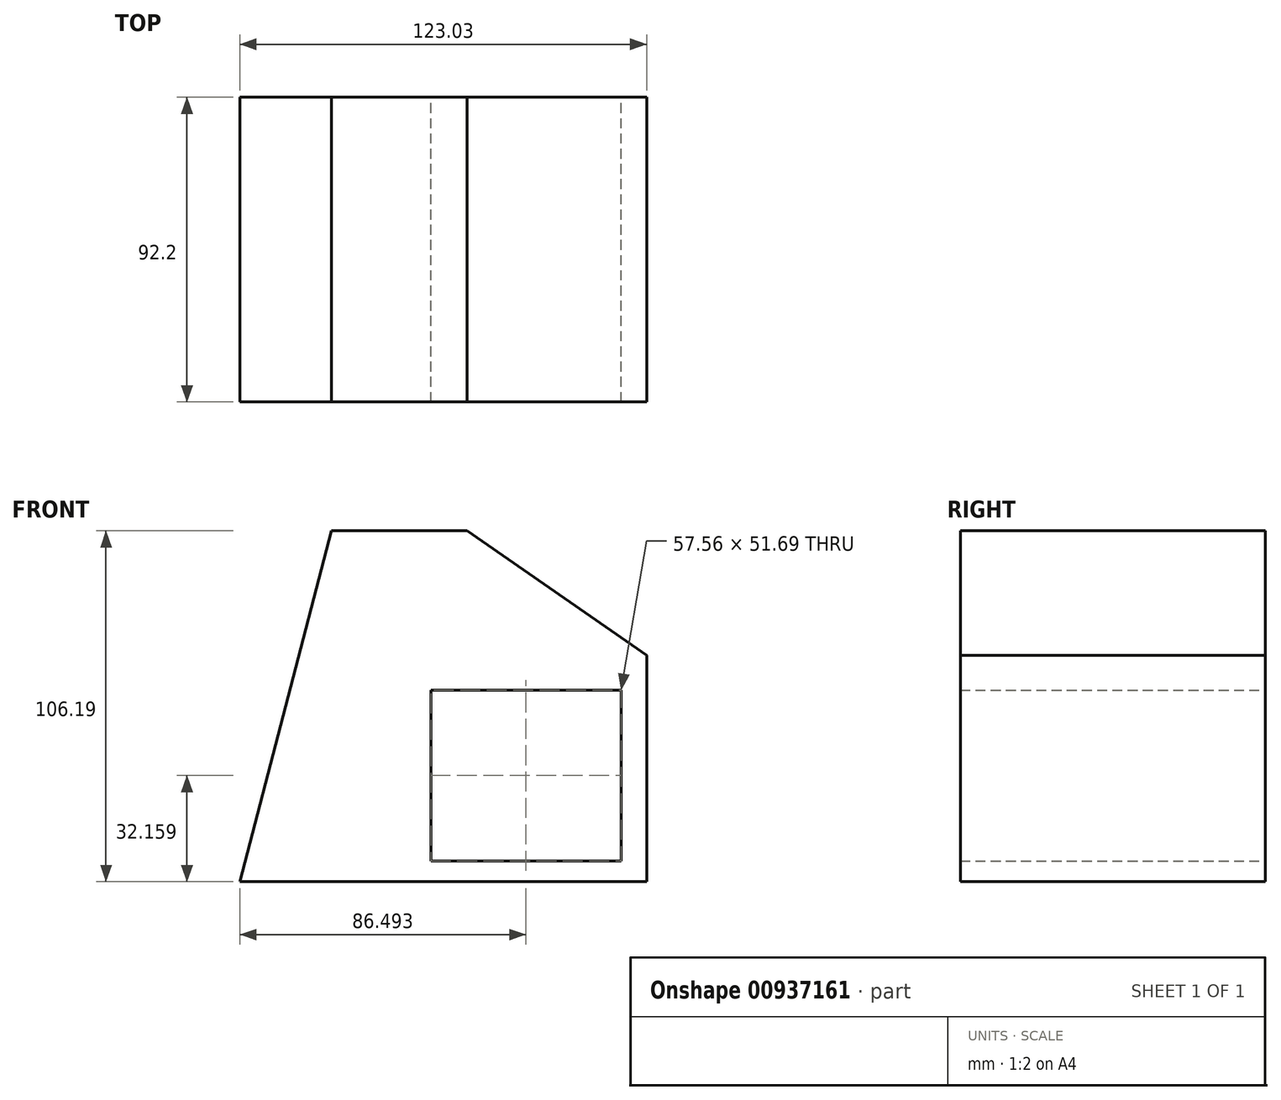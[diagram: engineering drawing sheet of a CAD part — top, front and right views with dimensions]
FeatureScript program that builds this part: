
annotation { "Feature Type Name" : "Feature", "Feature Type Description" : "" }
export const myFeature = defineFeature(function(context is Context, id is Id, definition is map)
    precondition{}
    {
        {
            var Q0;
            Q0=qCreatedBy(makeId("Front.planeOp"),FACE);
            var sketch = newSketch(context, id + "F0", { "sketchPlane" : qUnion([Q0])});
            skLineSegment(sketch, "E0", {"start": v(0, 0) * mm, "end": v(123.03, 0) * mm});
            skLineSegment(sketch, "E1", {"start": v(123.03, 0) * mm, "end": v(123.03, 68.54) * mm});
            skLineSegment(sketch, "E2", {"start": v(123.03, 68.54) * mm, "end": v(68.68, 106.19) * mm});
            skLineSegment(sketch, "E3", {"start": v(68.68, 106.19) * mm, "end": v(27.73, 106.19) * mm});
            skLineSegment(sketch, "E4", {"start": v(27.73, 106.19) * mm, "end": v(0, 0) * mm});
            skLineSegment(sketch, "E5.bottom", {"start": v(115.27, 6.31) * mm, "end": v(57.71, 6.31) * mm});
            skLineSegment(sketch, "E5.top", {"start": v(115.27, 58) * mm, "end": v(57.71, 58) * mm});
            skLineSegment(sketch, "E5.left", {"start": v(115.27, 6.31) * mm, "end": v(115.27, 58) * mm});
            skLineSegment(sketch, "E5.right", {"start": v(57.71, 6.31) * mm, "end": v(57.71, 58) * mm});
            skSolve(sketch);
        }
        {
            var Q0;
            Q0=makeQuery(id+"F0.imprint","IMPRINT",FACE,{"disambiguationData":[TD([[makeQuery(id+"F0.imprint","IMPRINT",EDGE,{"derivedFrom":sQuery(id+"F0.wireOp",EDGE,"E0")}),1.0]])]});
            extrude(context, id + "F1", {"entities" : qUnion([Q0]), "depth" : 92.2 * mm, "offsetDistance" : 25.4 * mm});
        }
    });
